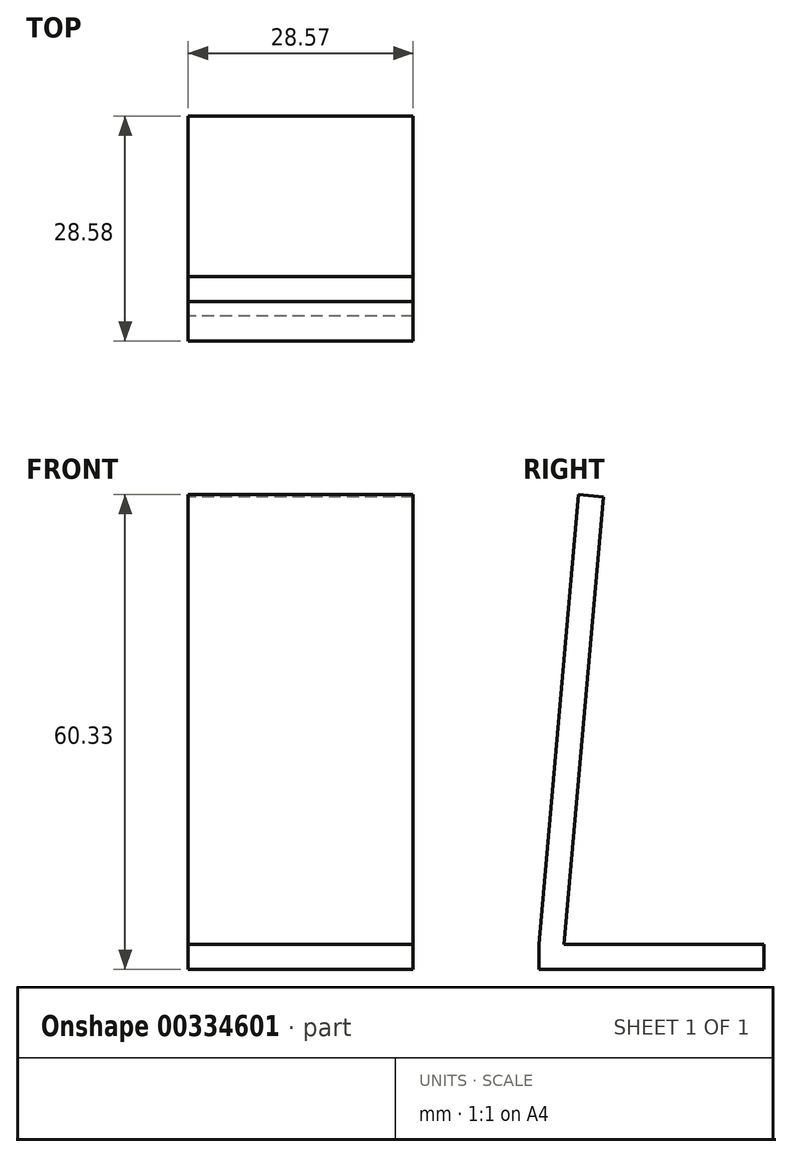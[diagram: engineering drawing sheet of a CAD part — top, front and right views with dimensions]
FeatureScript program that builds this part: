
annotation { "Feature Type Name" : "Feature", "Feature Type Description" : "" }
export const myFeature = defineFeature(function(context is Context, id is Id, definition is map)
    precondition{}
    {
        {
            var Q0;
            Q0=qCreatedBy(makeId("Right.planeOp"),FACE);
            var sketch = newSketch(context, id + "F0", { "sketchPlane" : qUnion([Q0])});
            skLineSegment(sketch, "E0", {"start": v(-14.29, 0) * mm, "end": v(14.29, 0) * mm});
            skLineSegment(sketch, "E1", {"start": v(14.29, 0) * mm, "end": v(14.29, 3.17) * mm});
            skLineSegment(sketch, "E2", {"start": v(14.29, 3.17) * mm, "end": v(-14.29, 3.17) * mm});
            skLineSegment(sketch, "E3", {"start": v(-14.29, 3.17) * mm, "end": v(-14.29, 0) * mm});
            skLineSegment(sketch, "E4", {"start": v(-5.01, 3.17) * mm, "end": v(-5.01, 60.33) * mm, "construction": true});
            skLineSegment(sketch, "E5", {"start": v(-14.29, 3.18) * mm, "end": v(-9.29, 60.33) * mm});
            skLineSegment(sketch, "E6", {"start": v(-9.29, 60.33) * mm, "end": v(-6.12, 60.05) * mm});
            skLineSegment(sketch, "E7", {"start": v(-6.12, 60.05) * mm, "end": v(-11.1, 3.18) * mm});
            skLineSegment(sketch, "E8", {"start": v(-11.1, 3.17) * mm, "end": v(-14.29, 3.17) * mm});
            skSolve(sketch);
        }
        {
            var Q0;
            Q0=qSketchRegion(id+"F0",true);
            extrude(context, id + "F1", {"entities" : qUnion([Q0]), "depth" : 28.57 * mm});
        }
    });
